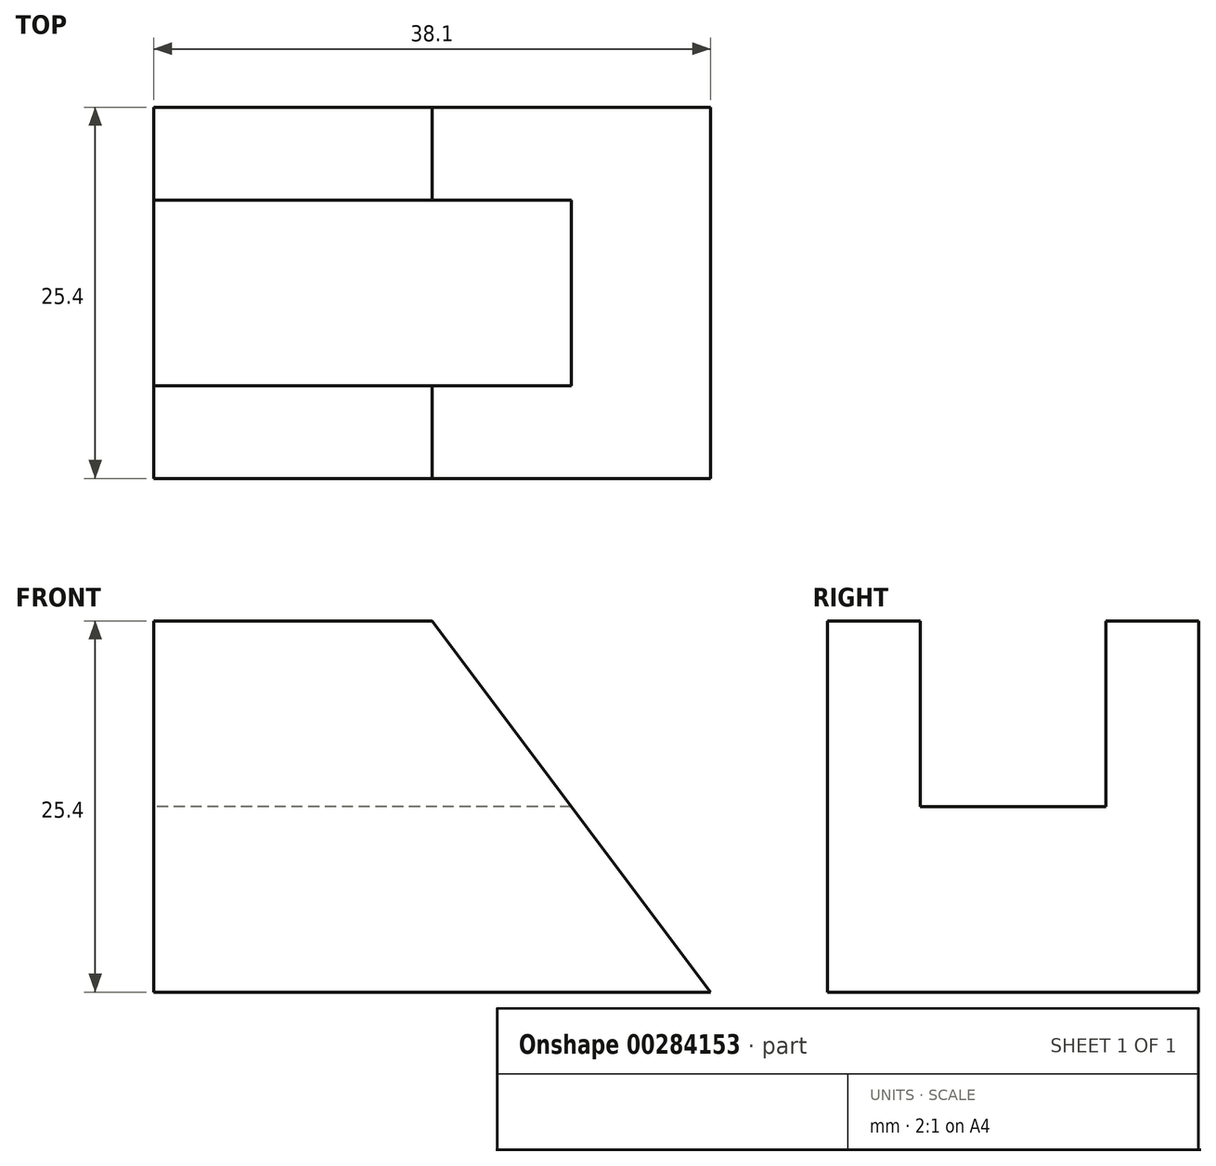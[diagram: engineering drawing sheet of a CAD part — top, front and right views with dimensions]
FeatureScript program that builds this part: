
annotation { "Feature Type Name" : "Feature", "Feature Type Description" : "" }
export const myFeature = defineFeature(function(context is Context, id is Id, definition is map)
    precondition{}
    {
        {
            var Q0;
            Q0=qCreatedBy(makeId("Front.planeOp"),FACE);
            var sketch = newSketch(context, id + "F0", { "sketchPlane" : qUnion([Q0])});
            skLineSegment(sketch, "E0", {"start": v(0, 0) * mm, "end": v(0, 25.4) * mm});
            skLineSegment(sketch, "E1", {"start": v(38.1, 0) * mm, "end": v(0, 0) * mm});
            skLineSegment(sketch, "E2", {"start": v(0, 25.4) * mm, "end": v(19.05, 25.4) * mm});
            skLineSegment(sketch, "E3", {"start": v(19.05, 25.4) * mm, "end": v(38.1, 0) * mm});
            skSolve(sketch);
        }
        {
            var Q0;
            Q0 = qSketchRegion(id + "F0", true);
            extrude(context, id + "F1", {"entities" : qUnion([Q0]), "endBound" : BoundingType.SYMMETRIC, "depth" : 25.4 * mm});
        }
        {
            var Q0;
            Q0=makeQuery(id+"F1.opExtrude","SWEPT_FACE",FACE,{"disambiguationData":[OSD([sQuery(id+"F0.wireOp",EDGE,"E0")])]});
            var sketch = newSketch(context, id + "F2", { "sketchPlane" : qUnion([Q0])});
            skSolve(sketch);
        }
        {
            var Q0;
            {var subQ0=sQuery(id+"F0.wireOp",EDGE,"E0");Q0=makeQuery(id+"F2.imprint","IMPRINT",FACE,{"disambiguationData":[TD([[makeQuery(id+"F2.imprint","IMPRINT",EDGE,{"derivedFrom":makeQuery(id+"F1.opExtrude","CAP_EDGE",EDGE,{"disambiguationData":[OSD([subQ0])],"isStart":true})}),-1.0]])]});}
            var sketch = newSketch(context, id + "F3", { "sketchPlane" : qUnion([Q0])});
            skLineSegment(sketch, "E4.bottom", {"start": v(-6.35, 25.4) * mm, "end": v(6.35, 25.4) * mm});
            skLineSegment(sketch, "E4.top", {"start": v(-6.35, 12.7) * mm, "end": v(6.35, 12.7) * mm});
            skLineSegment(sketch, "E4.left", {"start": v(-6.35, 25.4) * mm, "end": v(-6.35, 12.7) * mm});
            skLineSegment(sketch, "E4.right", {"start": v(6.35, 25.4) * mm, "end": v(6.35, 12.7) * mm});
            skSolve(sketch);
        }
        {
            var Q0;
            Q0 = qSketchRegion(id + "F3", true);
            extrude(context, id + "F4", {"entities" : qUnion([Q0]), "operationType" : NewBodyOperationType.REMOVE, "endBound" : BoundingType.THROUGH_ALL, "oppositeDirection" : true, "depth" : 25.4 * mm});
        }
    });
